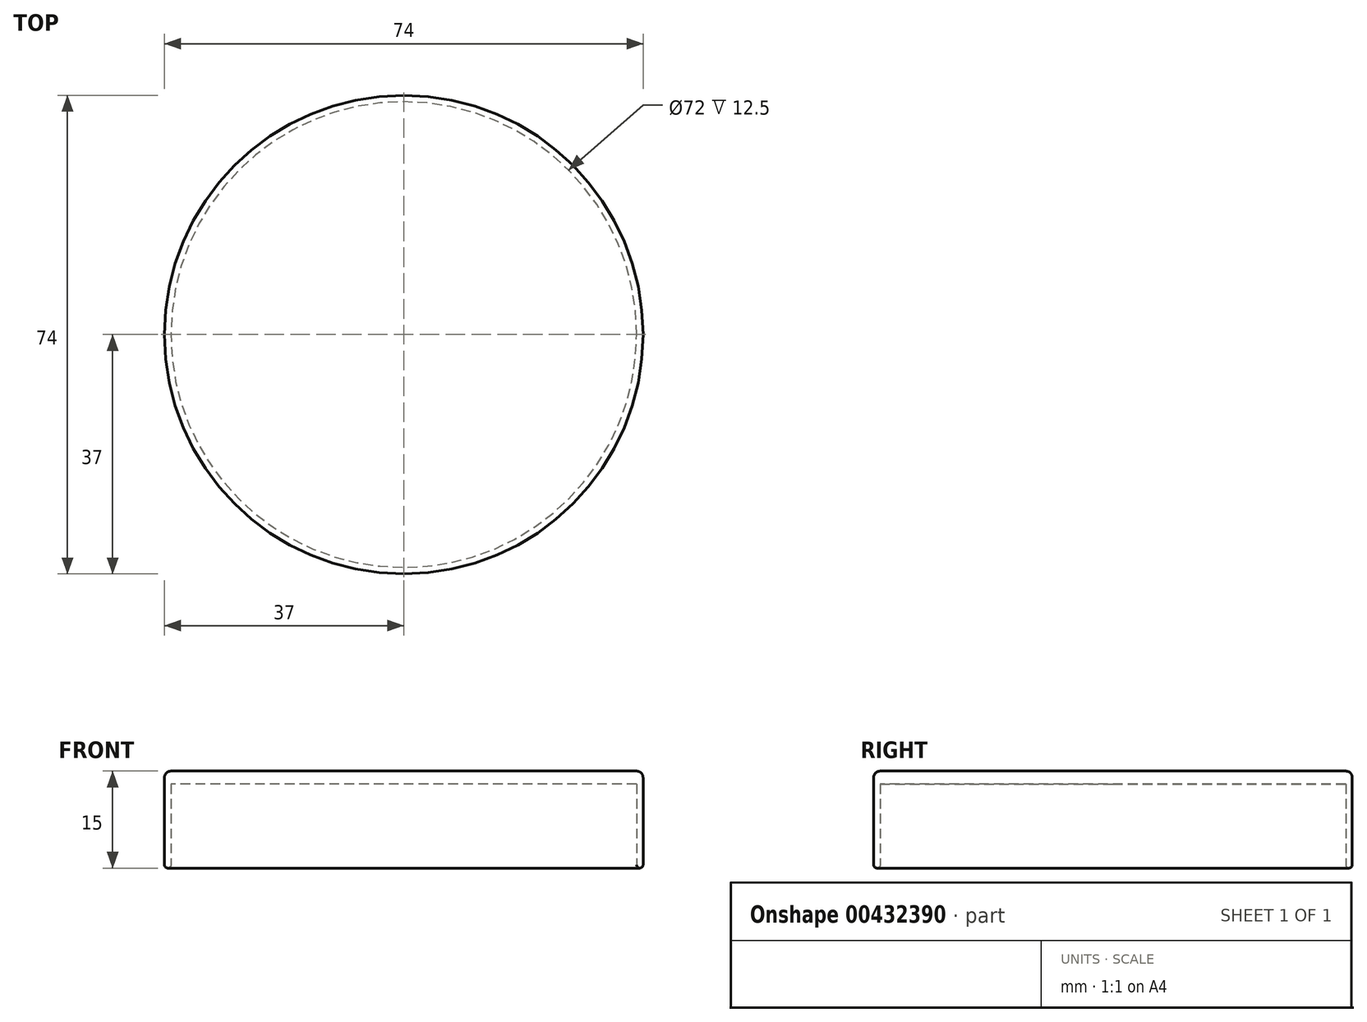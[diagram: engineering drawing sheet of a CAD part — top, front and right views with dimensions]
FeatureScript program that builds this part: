
annotation { "Feature Type Name" : "Feature", "Feature Type Description" : "" }
export const myFeature = defineFeature(function(context is Context, id is Id, definition is map)
    precondition{}
    {
        {
            var Q0;
            Q0=qCreatedBy(makeId("Top.planeOp"),FACE);
            var sketch = newSketch(context, id + "F0", { "sketchPlane" : qUnion([Q0])});
            skCircle(sketch, "E0", {"center": v(0, 0) * mm, "radius": 36 * mm});
            skCircle(sketch, "E1.0", {"center": v(0, 0) * mm, "radius": 37 * mm});
            skSolve(sketch);
        }
        {
            var Q0;
            Q0 = qSketchRegion(id + "F0", true);
            extrude(context, id + "F1", {"entities" : qUnion([Q0]), "depth" : 15 * mm});
        }
        {
            var Q0;
            Q0=makeQuery(id+"F1.opExtrude","CAP_FACE",FACE,{"disambiguationData":[OSD([sQuery(id+"F0.wireOp",EDGE,"E0"),sQuery(id+"F0.wireOp",EDGE,"E1.0")])],"isStart":false});
            var sketch = newSketch(context, id + "F2", { "sketchPlane" : qUnion([Q0])});
            skCircle(sketch, "E2", {"center": v(0, 0) * mm, "radius": 36.92 * mm});
            skSolve(sketch);
        }
        {
            var Q0;
            Q0 = qSketchRegion(id + "F2", true);
            extrude(context, id + "F3", {"entities" : qUnion([Q0]), "operationType" : NewBodyOperationType.ADD, "oppositeDirection" : true, "depth" : 2 * mm});
        }
        {
            var Q0;
            Q0=makeQuery(id+"F1.opExtrude","CAP_EDGE",EDGE,{"disambiguationData":[OSD([sQuery(id+"F0.wireOp",EDGE,"E1.0")])],"isStart":false});
            fillet(context, id + "F4", {"entities" : qUnion([Q0]), "radius" : 1 * mm, "tangentPropagation" : true, "allowEdgeOverflow" : false});
        }
        {
            var Q0;
            Q0=makeQuery(id+"F1.opExtrude","CAP_FACE",FACE,{"disambiguationData":[OSD([sQuery(id+"F0.wireOp",EDGE,"E0"),sQuery(id+"F0.wireOp",EDGE,"E1.0")])],"isStart":true});
            fillet(context, id + "F5", {"entities" : qUnion([Q0]), "radius" : .5 * mm, "tangentPropagation" : true, "allowEdgeOverflow" : false});
        }
    });
